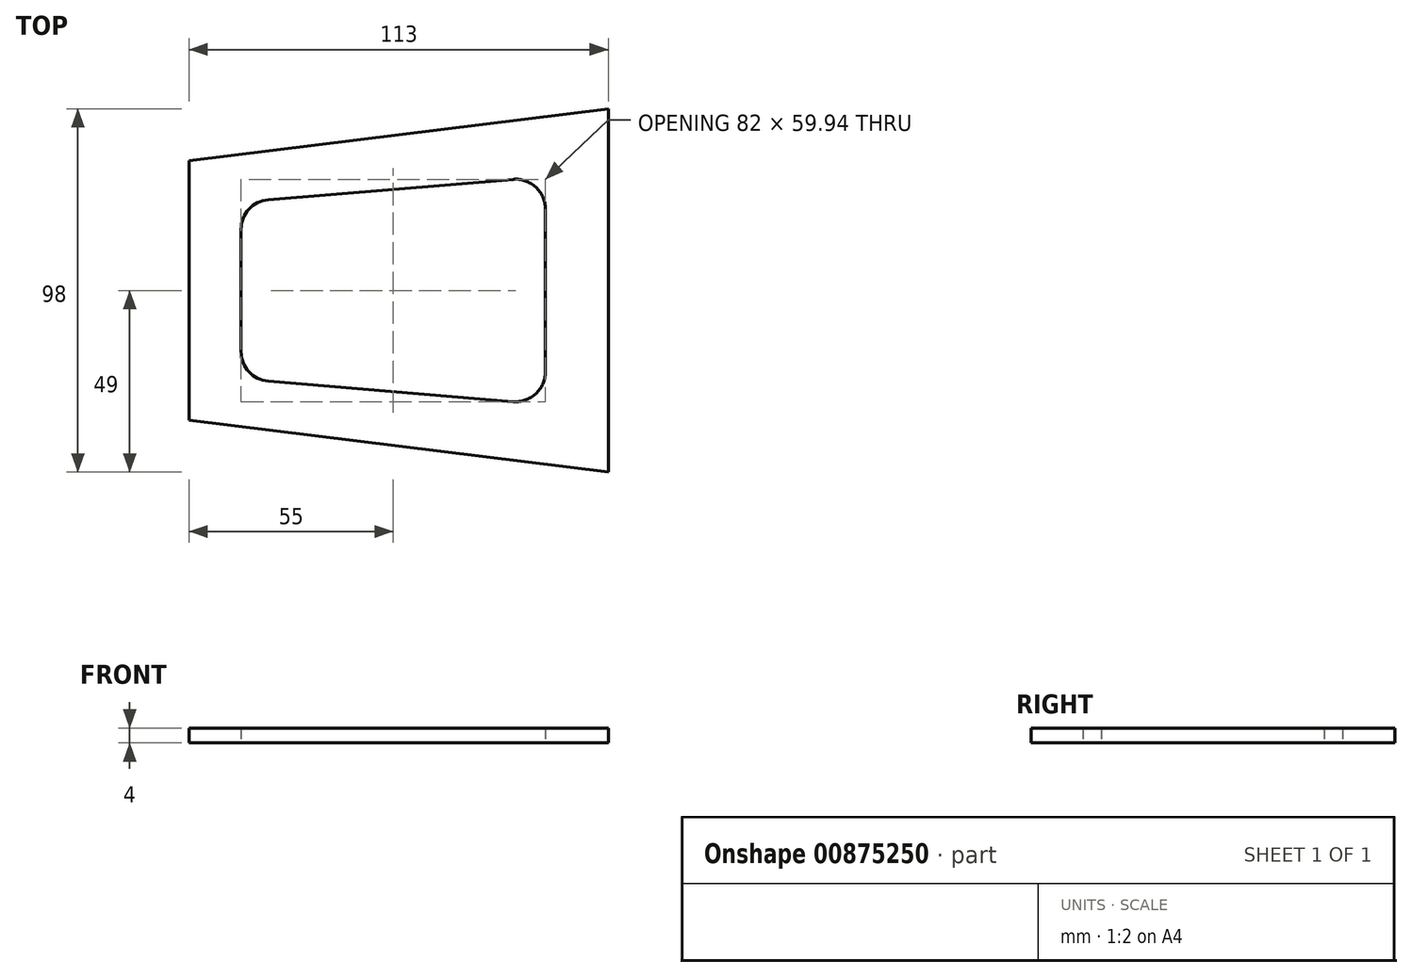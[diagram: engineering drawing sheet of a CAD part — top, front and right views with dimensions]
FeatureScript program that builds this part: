
annotation { "Feature Type Name" : "Feature", "Feature Type Description" : "" }
export const myFeature = defineFeature(function(context is Context, id is Id, definition is map)
    precondition{}
    {
        {
            var Q0;
            Q0=qCreatedBy(makeId("Top.planeOp"),FACE);
            var sketch = newSketch(context, id + "F0", { "sketchPlane" : qUnion([Q0])});
            skLineSegment(sketch, "E0", {"start": v(0, 35) * mm, "end": v(0, -35) * mm});
            skLineSegment(sketch, "E1", {"start": v(0, -35) * mm, "end": v(113, -49) * mm});
            skLineSegment(sketch, "E2", {"start": v(113, 49) * mm, "end": v(0, 35) * mm});
            skLineSegment(sketch, "E3", {"start": v(0, 0) * mm, "end": v(155, 0) * mm, "construction": true});
            skLineSegment(sketch, "E4", {"start": v(14, 16.5) * mm, "end": v(14, -16.5) * mm});
            skLineSegment(sketch, "E5", {"start": v(21.34, -24.47) * mm, "end": v(87.34, -29.97) * mm});
            skLineSegment(sketch, "E6", {"start": v(96, -22) * mm, "end": v(96, 22) * mm});
            skLineSegment(sketch, "E7", {"start": v(87.34, 29.97) * mm, "end": v(21.34, 24.47) * mm});
            skPoint(sketch, "E8.visualSharp", {"position": v(14, 23.86) * mm});
            skArc(sketch, "E8.filletArc", {"start": v(21.34, 24.47) * mm, "mid": v(16.11, 21.92) * mm, "end": v(14, 16.5) * mm});
            skPoint(sketch, "E9.visualSharp", {"position": v(96, 30.7) * mm});
            skArc(sketch, "E9.filletArc", {"start": v(96, 22) * mm, "mid": v(93.42, 27.89) * mm, "end": v(87.34, 29.97) * mm});
            skPoint(sketch, "E10.visualSharp", {"position": v(96, -30.7) * mm});
            skArc(sketch, "E10.filletArc", {"start": v(87.34, -29.97) * mm, "mid": v(93.42, -27.89) * mm, "end": v(96, -22) * mm});
            skPoint(sketch, "E11.visualSharp", {"position": v(14, -23.86) * mm});
            skArc(sketch, "E11.filletArc", {"start": v(14, -16.5) * mm, "mid": v(16.11, -21.92) * mm, "end": v(21.34, -24.47) * mm});
            skLineSegment(sketch, "E12", {"start": v(96, 0) * mm, "end": v(14, 0) * mm, "construction": true});
            skLineSegment(sketch, "E13", {"start": v(113, -49) * mm, "end": v(113, 49) * mm});
            skSolve(sketch);
        }
        {
            var Q0;
            Q0=qSketchRegion(id+"F0",true);
            extrude(context, id + "F1", {"entities" : qUnion([Q0]), "depth" : 4 * mm, "offsetDistance" : 25 * mm});
        }
    });
